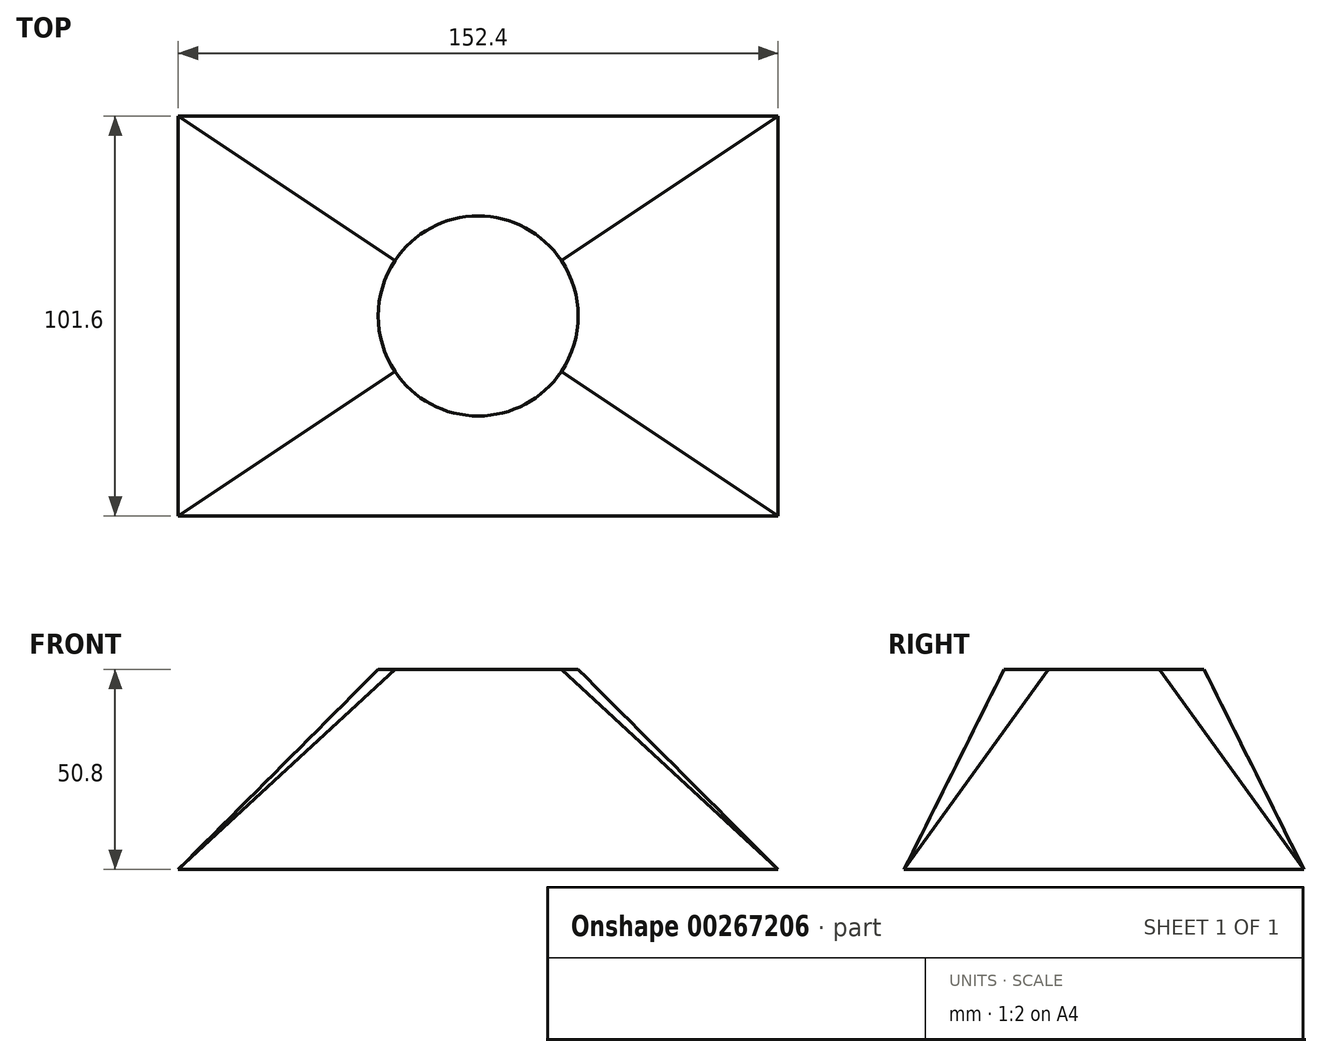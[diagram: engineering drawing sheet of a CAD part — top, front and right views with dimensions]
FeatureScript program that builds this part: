
annotation { "Feature Type Name" : "Feature", "Feature Type Description" : "" }
export const myFeature = defineFeature(function(context is Context, id is Id, definition is map)
    precondition{}
    {
        {
            var Q0;
            Q0=qCreatedBy(makeId("Top.planeOp"),FACE);
            var sketch = newSketch(context, id + "F0", { "sketchPlane" : qUnion([Q0])});
            skLineSegment(sketch, "E0.bottom", {"start": v(76.2, -50.8) * mm, "end": v(-76.2, -50.8) * mm});
            skLineSegment(sketch, "E0.top", {"start": v(76.2, 50.8) * mm, "end": v(-76.2, 50.8) * mm});
            skLineSegment(sketch, "E0.left", {"start": v(76.2, -50.8) * mm, "end": v(76.2, 50.8) * mm});
            skLineSegment(sketch, "E0.right", {"start": v(-76.2, -50.8) * mm, "end": v(-76.2, 50.8) * mm});
            skPoint(sketch, "E0.middle", {"position": v(0, 0) * mm});
            skSolve(sketch);
        }
        {
            var Q0;
            Q0=qCreatedBy(makeId("Top.planeOp"),FACE);
            cPlane(context, id + "F1", {"entities" : qUnion([Q0]), "cplaneType" : CPlaneType.OFFSET, "offset" : 50.8 * mm, "width" : 152.4 * mm, "height" : 152.4 * mm});
        }
        {
            var Q0;
            Q0=qCreatedBy(id+"F1.planeOp",FACE);
            var sketch = newSketch(context, id + "F2", { "sketchPlane" : qUnion([Q0])});
            skPoint(sketch, "E1.0", {"position": v(76.2, -50.8) * mm});
            skPoint(sketch, "E1.1", {"position": v(-76.2, -50.8) * mm});
            skPoint(sketch, "E1.2", {"position": v(-76.2, 50.8) * mm});
            skPoint(sketch, "E1.3", {"position": v(76.2, 50.8) * mm});
            skLineSegment(sketch, "E2", {"start": v(-76.2, -50.8) * mm, "end": v(76.2, 50.8) * mm, "construction": true});
            skLineSegment(sketch, "E3", {"start": v(-76.2, 50.8) * mm, "end": v(76.2, -50.8) * mm, "construction": true});
            skArc(sketch, "E4", {"start": v(-21.13, -14.09) * mm, "mid": v(0, -25.4) * mm, "end": v(21.13, -14.09) * mm});
            skArc(sketch, "E5", {"start": v(-21.13, 14.09) * mm, "mid": v(-25.4, 0) * mm, "end": v(-21.13, -14.09) * mm});
            skArc(sketch, "E6", {"start": v(21.13, 14.09) * mm, "mid": v(0, 25.4) * mm, "end": v(-21.13, 14.09) * mm});
            skArc(sketch, "E7", {"start": v(21.13, -14.09) * mm, "mid": v(25.4, 0) * mm, "end": v(21.13, 14.09) * mm});
            skSolve(sketch);
        }
        {
            var Q0;
            Q0=makeQuery(id+"F0.imprint","IMPRINT",FACE,{"disambiguationData":[TD([[makeQuery(id+"F0.imprint","IMPRINT",EDGE,{"derivedFrom":sQuery(id+"F0.wireOp",EDGE,"E0.bottom")}),-1.0]])]});
            var Q1;
            Q1=makeQuery(id+"F2.imprint","IMPRINT",FACE,{"disambiguationData":[TD([[makeQuery(id+"F2.imprint","IMPRINT",EDGE,{"derivedFrom":sQuery(id+"F2.wireOp",EDGE,"E4")}),1.0]])]});
            loft(context, id + "F3", {"sheetProfilesArray" : [{ "sheetProfileEntities" : qUnion([Q0]) }, { "sheetProfileEntities" : qUnion([Q1]) }]});
        }
    });
